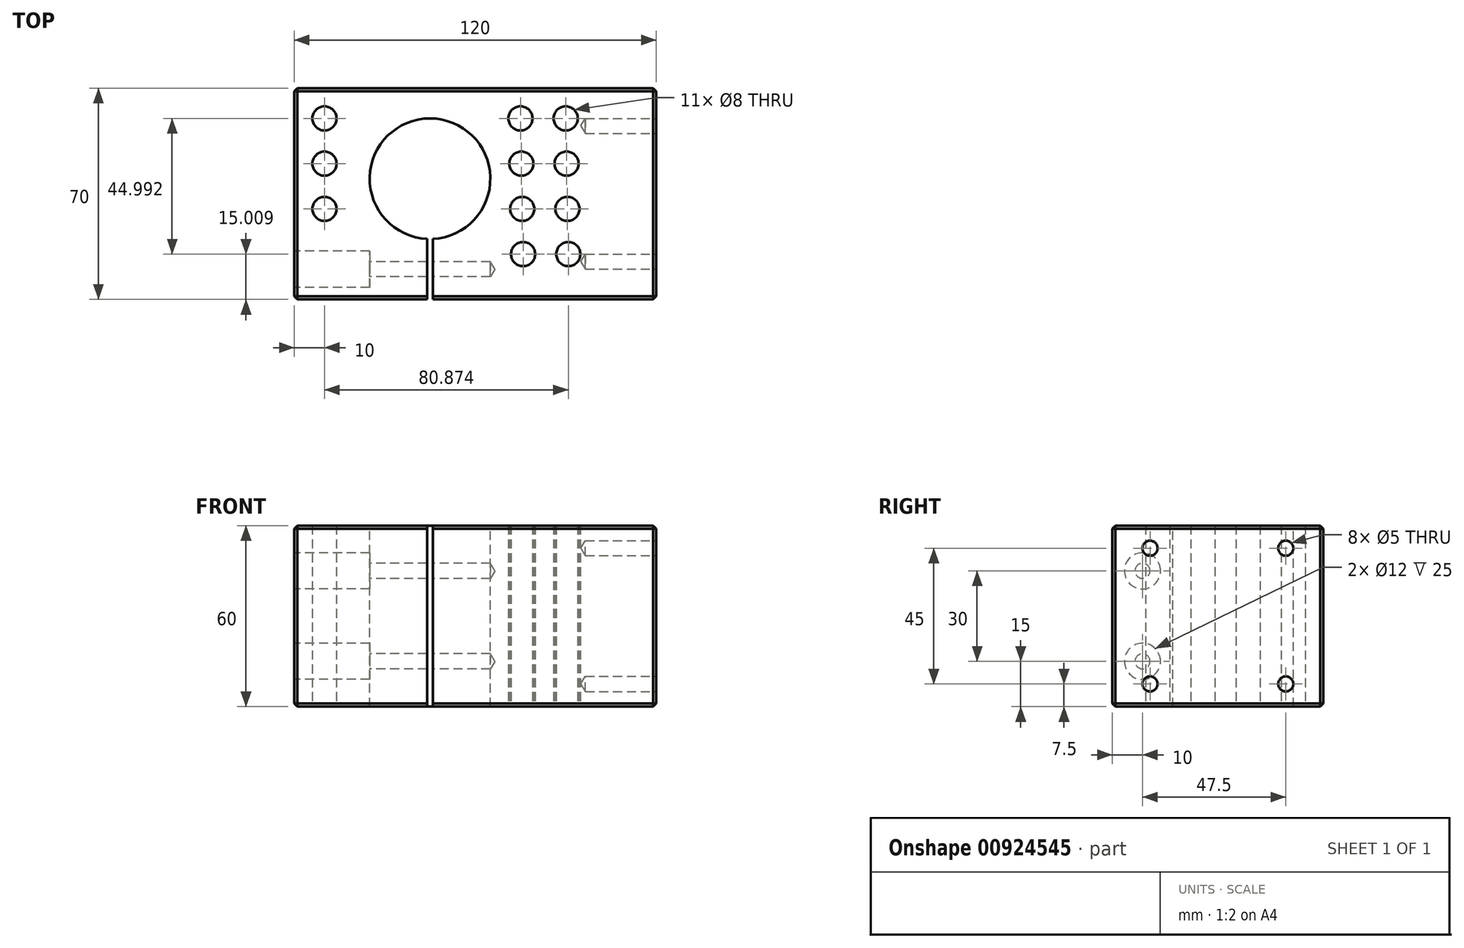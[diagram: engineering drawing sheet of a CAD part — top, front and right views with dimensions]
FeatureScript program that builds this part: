
annotation { "Feature Type Name" : "Feature", "Feature Type Description" : "" }
export const myFeature = defineFeature(function(context is Context, id is Id, definition is map)
    precondition{}
    {
        {
            var Q0;
            Q0=qCreatedBy(makeId("Top.planeOp"),FACE);
            var sketch = newSketch(context, id + "F0", { "sketchPlane" : qUnion([Q0])});
            skLineSegment(sketch, "E0.bottom", {"start": v(-60, 35) * mm, "end": v(60, 35) * mm});
            skLineSegment(sketch, "E0.top", {"start": v(-60, -35) * mm, "end": v(-16, -35) * mm});
            skLineSegment(sketch, "E0.left", {"start": v(-60, 35) * mm, "end": v(-60, -35) * mm});
            skLineSegment(sketch, "E0.right", {"start": v(60, 35) * mm, "end": v(60, -35) * mm});
            skArc(sketch, "E1", {"start": v(-14, -14.97) * mm, "mid": v(-15, 25) * mm, "end": v(-16, -14.97) * mm});
            skLineSegment(sketch, "E2", {"start": v(-15, 5) * mm, "end": v(-15, -46.53) * mm, "construction": true});
            skLineSegment(sketch, "E3", {"start": v(-16, -14.97) * mm, "end": v(-16, -35) * mm});
            skLineSegment(sketch, "E4", {"start": v(-14, -14.97) * mm, "end": v(-14, -35) * mm});
            skLineSegment(sketch, "E5.trimOffspring", {"start": v(-14, -35) * mm, "end": v(60, -35) * mm});
            skSolve(sketch);
        }
        {
            var Q0;
            Q0=makeQuery(id+"F0.imprint","IMPRINT",FACE,{"disambiguationData":[TD([[makeQuery(id+"F0.imprint","IMPRINT",EDGE,{"derivedFrom":sQuery(id+"F0.wireOp",EDGE,"E0.bottom")}),-1.0]])]});
            extrude(context, id + "F1", {"entities" : qUnion([Q0]), "oppositeDirection" : true, "depth" : 60 * mm, "offsetDistance" : 25 * mm});
        }
        {
            var Q0;
            Q0=makeQuery(id+"F1.opExtrude","SWEPT_FACE",FACE,{"disambiguationData":[OSD([sQuery(id+"F0.wireOp",EDGE,"E0.left")])]});
            var sketch = newSketch(context, id + "F2", { "sketchPlane" : qUnion([Q0])});
            skLineSegment(sketch, "E6.0", {"start": v(14.97, -60) * mm, "end": v(14.97, 0) * mm});
            skLineSegment(sketch, "E7", {"start": v(25, -57.27) * mm, "end": v(25, -6.23) * mm, "construction": true});
            skPoint(sketch, "E8", {"position": v(25, -45) * mm});
            skPoint(sketch, "E9", {"position": v(25, -15) * mm});
            skSolve(sketch);
        }
        {
            var Q0;
            Q0=sQuery(id+"F2.wireOp",VERTEX,"E8");
            var Q1;
            Q1=sQuery(id+"F2.wireOp",VERTEX,"E9");
            var Q2;
            Q2=makeQuery(id+"F1.opExtrude","SWEPT_BODY",BODY,{"disambiguationData":[OSD([sQuery(id+"F0.wireOp",EDGE,"E0.bottom"),sQuery(id+"F0.wireOp",EDGE,"E0.top"),sQuery(id+"F0.wireOp",EDGE,"E0.left"),sQuery(id+"F0.wireOp",EDGE,"E0.right"),sQuery(id+"F0.wireOp",EDGE,"E1"),sQuery(id+"F0.wireOp",EDGE,"E3"),sQuery(id+"F0.wireOp",EDGE,"E4"),sQuery(id+"F0.wireOp",EDGE,"E5.trimOffspring")])]});
            hole(context, id + "F3", {"style" : HoleStyle.C_BORE, "endStyle" : HoleEndStyle.BLIND, "holeDiameter" : 5 * mm, "cBoreDiameter" : 12 * mm, "cBoreDepth" : 25 * mm, "majorDiameter" : 5 * mm, "holeDepth" : 65 * mm, "isTappedThrough" : true, "tappedDepth" : 20.5 * mm, "tapClearance" : 3, "locations" : qUnion([Q0, Q1]), "scope" : qUnion([Q2])});
        }
        {
            var Q0;
            Q0=makeQuery(id+"F1.opExtrude","SWEPT_EDGE",EDGE,{"disambiguationData":[OSD([sQuery(id+"F0.wireOp",EDGE,"E0.top"),sQuery(id+"F0.wireOp",EDGE,"E0.left")])]});
            var Q1;
            Q1=makeQuery(id+"F1.opExtrude","SWEPT_EDGE",EDGE,{"disambiguationData":[OSD([sQuery(id+"F0.wireOp",EDGE,"E0.bottom"),sQuery(id+"F0.wireOp",EDGE,"E0.left")])]});
            var Q2;
            Q2=makeQuery(id+"F1.opExtrude","SWEPT_EDGE",EDGE,{"disambiguationData":[OSD([sQuery(id+"F0.wireOp",EDGE,"E0.right"),sQuery(id+"F0.wireOp",EDGE,"E5.trimOffspring")])]});
            var Q3;
            Q3=makeQuery(id+"F1.opExtrude","SWEPT_EDGE",EDGE,{"disambiguationData":[OSD([sQuery(id+"F0.wireOp",EDGE,"E0.bottom"),sQuery(id+"F0.wireOp",EDGE,"E0.right")])]});
            var Q4;
            Q4=makeQuery(id+"F1.opExtrude","CAP_EDGE",EDGE,{"disambiguationData":[OSD([sQuery(id+"F0.wireOp",EDGE,"E0.bottom")])],"isStart":false});
            var Q5;
            Q5=makeQuery(id+"F1.opExtrude","CAP_EDGE",EDGE,{"disambiguationData":[OSD([sQuery(id+"F0.wireOp",EDGE,"E0.left")])],"isStart":false});
            var Q6;
            Q6=makeQuery(id+"F1.opExtrude","CAP_EDGE",EDGE,{"disambiguationData":[OSD([sQuery(id+"F0.wireOp",EDGE,"E0.top")])],"isStart":false});
            var Q7;
            Q7=makeQuery(id+"F1.opExtrude","CAP_EDGE",EDGE,{"disambiguationData":[OSD([sQuery(id+"F0.wireOp",EDGE,"E5.trimOffspring")])],"isStart":false});
            var Q8;
            Q8=makeQuery(id+"F1.opExtrude","CAP_EDGE",EDGE,{"disambiguationData":[OSD([sQuery(id+"F0.wireOp",EDGE,"E0.right")])],"isStart":false});
            var Q9;
            Q9=makeQuery(id+"F1.opExtrude","CAP_EDGE",EDGE,{"disambiguationData":[OSD([sQuery(id+"F0.wireOp",EDGE,"E0.left")])],"isStart":true});
            var Q10;
            Q10=makeQuery(id+"F1.opExtrude","CAP_EDGE",EDGE,{"disambiguationData":[OSD([sQuery(id+"F0.wireOp",EDGE,"E0.top")])],"isStart":true});
            var Q11;
            Q11=makeQuery(id+"F1.opExtrude","CAP_EDGE",EDGE,{"disambiguationData":[OSD([sQuery(id+"F0.wireOp",EDGE,"E5.trimOffspring")])],"isStart":true});
            var Q12;
            Q12=makeQuery(id+"F1.opExtrude","CAP_EDGE",EDGE,{"disambiguationData":[OSD([sQuery(id+"F0.wireOp",EDGE,"E0.right")])],"isStart":true});
            var Q13;
            Q13=makeQuery(id+"F1.opExtrude","CAP_EDGE",EDGE,{"disambiguationData":[OSD([sQuery(id+"F0.wireOp",EDGE,"E0.bottom")])],"isStart":true});
            chamfer(context, id + "F4", {"entities" : qUnion([Q0, Q1, Q2, Q3, Q4, Q5, Q6, Q7, Q8, Q9, Q10, Q11, Q12, Q13]), "width" : 1 * mm, "tangentPropagation" : true});
        }
        {
            var Q0;
            Q0=makeQuery(id+"F1.opExtrude","SWEPT_FACE",FACE,{"disambiguationData":[OSD([sQuery(id+"F0.wireOp",EDGE,"E0.right")])]});
            var sketch = newSketch(context, id + "F5", { "sketchPlane" : qUnion([Q0])});
            skLineSegment(sketch, "E10.bottom", {"start": v(-22.5, -7.5) * mm, "end": v(22.5, -7.5) * mm, "construction": true});
            skLineSegment(sketch, "E10.top", {"start": v(-22.5, -52.5) * mm, "end": v(22.5, -52.5) * mm, "construction": true});
            skLineSegment(sketch, "E10.left", {"start": v(-22.5, -7.5) * mm, "end": v(-22.5, -52.5) * mm, "construction": true});
            skLineSegment(sketch, "E10.right", {"start": v(22.5, -7.5) * mm, "end": v(22.5, -52.5) * mm, "construction": true});
            skSolve(sketch);
        }
        {
            var Q0;
            Q0=sQuery(id+"F5.wireOp",VERTEX,"E10.bottom.start");
            var Q1;
            Q1=sQuery(id+"F5.wireOp",VERTEX,"E10.bottom.end");
            var Q2;
            Q2=sQuery(id+"F5.wireOp",VERTEX,"E10.top.end");
            var Q3;
            Q3=sQuery(id+"F5.wireOp",VERTEX,"E10.top.start");
            var Q4;
            Q4=makeQuery(id+"F1.opExtrude","SWEPT_BODY",BODY,{"disambiguationData":[OSD([sQuery(id+"F0.wireOp",EDGE,"E0.bottom"),sQuery(id+"F0.wireOp",EDGE,"E0.top"),sQuery(id+"F0.wireOp",EDGE,"E0.left"),sQuery(id+"F0.wireOp",EDGE,"E0.right"),sQuery(id+"F0.wireOp",EDGE,"E1"),sQuery(id+"F0.wireOp",EDGE,"E3"),sQuery(id+"F0.wireOp",EDGE,"E4"),sQuery(id+"F0.wireOp",EDGE,"E5.trimOffspring")])]});
            hole(context, id + "F6", {"style" : HoleStyle.SIMPLE, "endStyle" : HoleEndStyle.BLIND, "standardTappedOrClearance" : lookupTablePath({ "standard" : "ISO", "engagement" : "75%", "pitch" : "1 mm", "size" : "M6", "type" : "Tapped" }), "standardBlindInLast" : lookupTablePath({ "standard" : "ISO", "engagement" : "75%", "pitch" : "1 mm", "size" : "M6", "type" : "Tapped" }), "holeDiameter" : 5 * mm, "majorDiameter" : 6 * mm, "showTappedDepth" : true, "holeDepth" : 23.5 * mm, "isTappedThrough" : true, "tappedDepth" : 20.5 * mm, "tapClearance" : 3, "locations" : qUnion([Q0, Q1, Q2, Q3]), "scope" : qUnion([Q4])});
        }
        {
            var Q0;
            Q0=makeQuery(id+"F1.opExtrude","CAP_FACE",FACE,{"disambiguationData":[OSD([sQuery(id+"F0.wireOp",EDGE,"E0.bottom"),sQuery(id+"F0.wireOp",EDGE,"E0.top"),sQuery(id+"F0.wireOp",EDGE,"E0.left"),sQuery(id+"F0.wireOp",EDGE,"E0.right"),sQuery(id+"F0.wireOp",EDGE,"E1"),sQuery(id+"F0.wireOp",EDGE,"E3"),sQuery(id+"F0.wireOp",EDGE,"E4"),sQuery(id+"F0.wireOp",EDGE,"E5.trimOffspring")])],"isStart":false});
            var sketch = newSketch(context, id + "F7", { "sketchPlane" : qUnion([Q0])});
            skPoint(sketch, "E11", {"position": v(-50, -25) * mm});
            skPoint(sketch, "E12", {"position": v(-50, -10) * mm});
            skPoint(sketch, "E13", {"position": v(-50, 5) * mm});
            skPoint(sketch, "E14", {"position": v(-50, 20) * mm});
            skSolve(sketch);
        }
        {
            var Q0;
            Q0=makeQuery(id+"F1.opExtrude","CAP_FACE",FACE,{"disambiguationData":[OSD([sQuery(id+"F0.wireOp",EDGE,"E0.bottom"),sQuery(id+"F0.wireOp",EDGE,"E0.top"),sQuery(id+"F0.wireOp",EDGE,"E0.left"),sQuery(id+"F0.wireOp",EDGE,"E0.right"),sQuery(id+"F0.wireOp",EDGE,"E1"),sQuery(id+"F0.wireOp",EDGE,"E3"),sQuery(id+"F0.wireOp",EDGE,"E4"),sQuery(id+"F0.wireOp",EDGE,"E5.trimOffspring")])],"isStart":false});
            var sketch = newSketch(context, id + "F8", { "sketchPlane" : qUnion([Q0])});
            skPoint(sketch, "E15", {"position": v(15, -25) * mm});
            skPoint(sketch, "E16.0.1.0", {"position": v(15.3, -10) * mm});
            skPoint(sketch, "E16.0.2.0", {"position": v(15.58, 5) * mm});
            skPoint(sketch, "E16.0.3.0", {"position": v(15.87, 20) * mm});
            skPoint(sketch, "E16.1.0.0", {"position": v(30, -25) * mm});
            skPoint(sketch, "E16.1.1.0", {"position": v(30.3, -10) * mm});
            skPoint(sketch, "E16.1.2.0", {"position": v(30.58, 5) * mm});
            skPoint(sketch, "E16.1.3.0", {"position": v(30.87, 20) * mm});
            skLineSegment(sketch, "E16.direction1", {"start": v(15, -25) * mm, "end": v(30, -25) * mm, "construction": true});
            skLineSegment(sketch, "E16.direction2", {"start": v(15, -25) * mm, "end": v(15.3, -10) * mm, "construction": true});
            skSolve(sketch);
        }
        {
            var Q0;
            Q0=sQuery(id+"F8.wireOp",VERTEX,"E15");
            var Q1;
            Q1=sQuery(id+"F8.wireOp",VERTEX,"E16.0.1.0");
            var Q2;
            Q2=sQuery(id+"F8.wireOp",VERTEX,"E16.0.2.0");
            var Q3;
            Q3=sQuery(id+"F8.wireOp",VERTEX,"E16.0.3.0");
            var Q4;
            Q4=sQuery(id+"F8.wireOp",VERTEX,"E16.1.3.0");
            var Q5;
            Q5=sQuery(id+"F8.wireOp",VERTEX,"E16.1.2.0");
            var Q6;
            Q6=sQuery(id+"F8.wireOp",VERTEX,"E16.1.1.0");
            var Q7;
            Q7=sQuery(id+"F8.wireOp",VERTEX,"E16.1.0.0");
            var Q8;
            Q8=sQuery(id+"F7.wireOp",VERTEX,"E11");
            var Q9;
            Q9=sQuery(id+"F7.wireOp",VERTEX,"E12");
            var Q10;
            Q10=sQuery(id+"F7.wireOp",VERTEX,"E13");
            var Q11;
            Q11=makeQuery(id+"F1.opExtrude","SWEPT_BODY",BODY,{"disambiguationData":[OSD([sQuery(id+"F0.wireOp",EDGE,"E0.bottom"),sQuery(id+"F0.wireOp",EDGE,"E0.top"),sQuery(id+"F0.wireOp",EDGE,"E0.left"),sQuery(id+"F0.wireOp",EDGE,"E0.right"),sQuery(id+"F0.wireOp",EDGE,"E1"),sQuery(id+"F0.wireOp",EDGE,"E3"),sQuery(id+"F0.wireOp",EDGE,"E4"),sQuery(id+"F0.wireOp",EDGE,"E5.trimOffspring")])]});
            hole(context, id + "F9", {"style" : HoleStyle.SIMPLE, "endStyle" : HoleEndStyle.THROUGH, "holeDiameter" : 8 * mm, "majorDiameter" : 6 * mm, "isTappedThrough" : true, "tappedDepth" : 20.5 * mm, "tapClearance" : 3, "locations" : qUnion([Q0, Q1, Q2, Q3, Q4, Q5, Q6, Q7, Q8, Q9, Q10]), "scope" : qUnion([Q11])});
        }
    });
